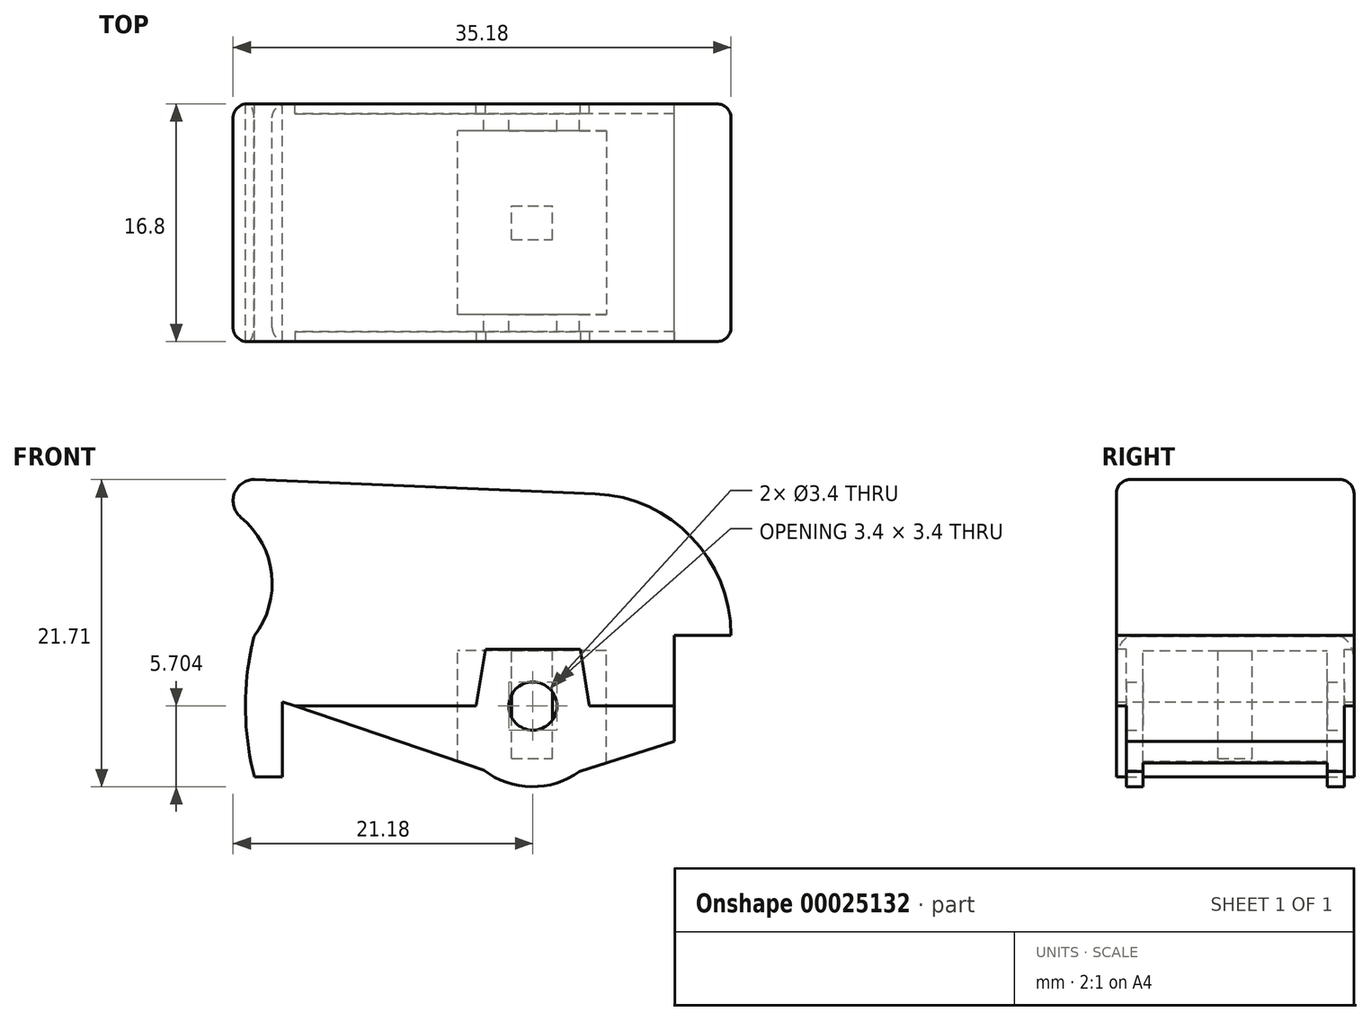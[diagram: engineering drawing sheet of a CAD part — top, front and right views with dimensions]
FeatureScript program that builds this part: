
annotation { "Feature Type Name" : "Feature", "Feature Type Description" : "" }
export const myFeature = defineFeature(function(context is Context, id is Id, definition is map)
    precondition{}
    {
        {
            var Q0;
            Q0=qCreatedBy(makeId("Front.planeOp"),FACE);
            var sketch = newSketch(context, id + "F0", { "sketchPlane" : qUnion([Q0])});
            skLineSegment(sketch, "E0", {"start": v(-33.61, 31.26) * mm, "end": v(-9.6, 30.25) * mm});
            skArc(sketch, "E1", {"start": v(0, 20.25) * mm, "mid": v(-2.78, 27.18) * mm, "end": v(-9.6, 30.25) * mm});
            skLineSegment(sketch, "E2", {"start": v(0, 20.25) * mm, "end": v(-4, 20.25) * mm});
            skLineSegment(sketch, "E3", {"start": v(-4, 20.25) * mm, "end": v(-4, 12.75) * mm});
            skLineSegment(sketch, "E4", {"start": v(-4, 15.25) * mm, "end": v(-26.9, 15.25) * mm, "construction": true});
            skCircle(sketch, "E5", {"center": v(-14, 15.25) * mm, "radius": 1.7 * mm});
            skArc(sketch, "E6", {"start": v(-33.7, 20.18) * mm, "mid": v(-34.3, 15.22) * mm, "end": v(-33.68, 10.26) * mm});
            skArc(sketch, "E7.0", {"start": v(-17.47, 10.73) * mm, "mid": v(-14.1, 9.55) * mm, "end": v(-10.7, 10.61) * mm});
            skPoint(sketch, "E8.visualSharp", {"position": v(-29.1, 31.07) * mm});
            skArc(sketch, "E8.filletArc", {"start": v(-33.61, 31.26) * mm, "mid": v(-35.08, 30.3) * mm, "end": v(-34.63, 28.6) * mm});
            skArc(sketch, "E9", {"start": v(-34.63, 28.6) * mm, "mid": v(-32.45, 24.58) * mm, "end": v(-33.7, 20.18) * mm});
            skLineSegment(sketch, "E10", {"start": v(-33.61, 31.26) * mm, "end": v(-33.68, 10.26) * mm, "construction": true});
            skLineSegment(sketch, "E11", {"start": v(-33.68, 10.26) * mm, "end": v(-31.68, 10.25) * mm});
            skLineSegment(sketch, "E12", {"start": v(-31.68, 10.25) * mm, "end": v(-31.68, 15.55) * mm});
            skLineSegment(sketch, "E13", {"start": v(-31.68, 15.55) * mm, "end": v(-17.47, 10.73) * mm});
            skLineSegment(sketch, "E14", {"start": v(-4, 12.75) * mm, "end": v(-10.7, 10.61) * mm});
            skPoint(sketch, "E15.orphan", {"position": v(-14, 9.55) * mm});
            skSolve(sketch);
        }
        {
            var Q0;
            Q0=makeQuery(id+"F0.imprint","IMPRINT",FACE,{"disambiguationData":[TD([[makeQuery(id+"F0.imprint","IMPRINT",EDGE,{"derivedFrom":sQuery(id+"F0.wireOp",EDGE,"E0")}),-1.0]])]});
            extrude(context, id + "F1", {"entities" : qUnion([Q0]), "depth" : 16.8 / 2 * mm, "hasSecondDirection" : true, "secondDirectionOppositeDirection" : true, "secondDirectionDepth" : (16.8 / 2) * mm});
        }
        {
            var Q0;
            Q0=makeQuery(id+"F1.opExtrude","CAP_FACE",FACE,{"disambiguationData":[OSD([sQuery(id+"F0.wireOp",EDGE,"E0"),sQuery(id+"F0.wireOp",EDGE,"E1"),sQuery(id+"F0.wireOp",EDGE,"E2"),sQuery(id+"F0.wireOp",EDGE,"E3"),sQuery(id+"F0.wireOp",EDGE,"E5"),sQuery(id+"F0.wireOp",EDGE,"E6"),sQuery(id+"F0.wireOp",EDGE,"E7.0"),sQuery(id+"F0.wireOp",EDGE,"E8.filletArc"),sQuery(id+"F0.wireOp",EDGE,"E9"),sQuery(id+"F0.wireOp",EDGE,"E11"),sQuery(id+"F0.wireOp",EDGE,"E12"),sQuery(id+"F0.wireOp",EDGE,"E13"),sQuery(id+"F0.wireOp",EDGE,"E14")])],"isStart":false});
            var sketch = newSketch(context, id + "F2", { "sketchPlane" : qUnion([Q0])});
            skLineSegment(sketch, "E16", {"start": v(-4, 15.25) * mm, "end": v(-10, 15.25) * mm});
            skLineSegment(sketch, "E17", {"start": v(-10, 15.25) * mm, "end": v(-10.65, 19.25) * mm});
            skLineSegment(sketch, "E18", {"start": v(-10.65, 19.25) * mm, "end": v(-17.35, 19.25) * mm});
            skLineSegment(sketch, "E19", {"start": v(-17.35, 19.25) * mm, "end": v(-18, 15.25) * mm});
            skLineSegment(sketch, "E20", {"start": v(-18, 15.25) * mm, "end": v(-30.8, 15.25) * mm});
            skLineSegment(sketch, "E21", {"start": v(-14, 15.25) * mm, "end": v(-14, 19.25) * mm, "construction": true});
            skSolve(sketch);
        }
        {
            var Q0;
            {var subQ4=sQuery(id+"F2.wireOp",EDGE,"E16");Q0=makeQuery(id+"F2.imprint","IMPRINT",FACE,{"disambiguationData":[TD([[makeQuery(id+"F2.imprint","IMPRINT",EDGE,{"derivedFrom":subQ4}),1.0]])]});}
            extrude(context, id + "F3", {"entities" : qUnion([Q0]), "oppositeDirection" : true, "depth" : 0.7 * mm});
        }
        {
            var Q0;
            Q0=makeQuery(id+"F3.opExtrude","SWEPT_BODY",BODY,{"disambiguationData":[OSD([sQuery(id+"F0.wireOp",EDGE,"E3"),sQuery(id+"F0.wireOp",EDGE,"E5"),sQuery(id+"F0.wireOp",EDGE,"E7.0"),sQuery(id+"F0.wireOp",EDGE,"E13"),sQuery(id+"F0.wireOp",EDGE,"E14"),sQuery(id+"F2.wireOp",EDGE,"E16"),sQuery(id+"F2.wireOp",EDGE,"E17"),sQuery(id+"F2.wireOp",EDGE,"E18"),sQuery(id+"F2.wireOp",EDGE,"E19"),sQuery(id+"F2.wireOp",EDGE,"E20")])]});
            var Q1;
            Q1=qCreatedBy(makeId("Front.planeOp"),FACE);
            mirror(context, id + "F4", {"entities" : qUnion([Q0]), "mirrorPlane" : qUnion([Q1])});
        }
        {
            var Q0;
            Q0=makeQuery(id+"F3.opExtrude","SWEPT_BODY",BODY,{"disambiguationData":[OSD([sQuery(id+"F0.wireOp",EDGE,"E3"),sQuery(id+"F0.wireOp",EDGE,"E5"),sQuery(id+"F0.wireOp",EDGE,"E7.0"),sQuery(id+"F0.wireOp",EDGE,"E13"),sQuery(id+"F0.wireOp",EDGE,"E14"),sQuery(id+"F2.wireOp",EDGE,"E16"),sQuery(id+"F2.wireOp",EDGE,"E17"),sQuery(id+"F2.wireOp",EDGE,"E18"),sQuery(id+"F2.wireOp",EDGE,"E19"),sQuery(id+"F2.wireOp",EDGE,"E20")])]});
            var Q1;
            Q1=makeQuery(id+"F4.opPattern","COPY",BODY,{"derivedFrom":makeQuery(id+"F3.opExtrude","SWEPT_BODY",BODY,{"disambiguationData":[OSD([sQuery(id+"F0.wireOp",EDGE,"E3"),sQuery(id+"F0.wireOp",EDGE,"E5"),sQuery(id+"F0.wireOp",EDGE,"E7.0"),sQuery(id+"F0.wireOp",EDGE,"E13"),sQuery(id+"F0.wireOp",EDGE,"E14"),sQuery(id+"F2.wireOp",EDGE,"E16"),sQuery(id+"F2.wireOp",EDGE,"E17"),sQuery(id+"F2.wireOp",EDGE,"E18"),sQuery(id+"F2.wireOp",EDGE,"E19"),sQuery(id+"F2.wireOp",EDGE,"E20")])]}),"instanceName":"1"});
            var Q2;
            Q2=makeQuery(id+"F1.opExtrude","SWEPT_BODY",BODY,{"disambiguationData":[OSD([sQuery(id+"F0.wireOp",EDGE,"E0"),sQuery(id+"F0.wireOp",EDGE,"E1"),sQuery(id+"F0.wireOp",EDGE,"E2"),sQuery(id+"F0.wireOp",EDGE,"E3"),sQuery(id+"F0.wireOp",EDGE,"E5"),sQuery(id+"F0.wireOp",EDGE,"E6"),sQuery(id+"F0.wireOp",EDGE,"E7.0"),sQuery(id+"F0.wireOp",EDGE,"E8.filletArc"),sQuery(id+"F0.wireOp",EDGE,"E9"),sQuery(id+"F0.wireOp",EDGE,"E11"),sQuery(id+"F0.wireOp",EDGE,"E12"),sQuery(id+"F0.wireOp",EDGE,"E13"),sQuery(id+"F0.wireOp",EDGE,"E14")])]});
            booleanBodies(context, id + "F5", {"operationType" : BooleanOperationType.SUBTRACTION, "tools" : qUnion([Q0, Q1]), "targets" : qUnion([Q2])});
        }
        {
            var Q0;
            Q0=makeQuery(id+"F5.opBoolean","COPY",FACE,{"derivedFrom":makeQuery(id+"F3.opExtrude","SWEPT_FACE",FACE,{"disambiguationData":[OSD([sQuery(id+"F2.wireOp",EDGE,"E16")])]})});
            var sketch = newSketch(context, id + "F6", { "sketchPlane" : qUnion([Q0])});
            skLineSegment(sketch, "E22.bottom", {"start": v(-8.8, 6.5) * mm, "end": v(-19.3, 6.5) * mm});
            skLineSegment(sketch, "E22.top", {"start": v(-8.8, -6.5) * mm, "end": v(-19.3, -6.5) * mm});
            skLineSegment(sketch, "E22.left", {"start": v(-8.8, 6.5) * mm, "end": v(-8.8, -6.5) * mm});
            skLineSegment(sketch, "E22.right", {"start": v(-19.3, 6.5) * mm, "end": v(-19.3, -6.5) * mm});
            skSolve(sketch);
        }
        {
            var Q0;
            Q0 = qSketchRegion(id + "F6", true);
            extrude(context, id + "F7", {"entities" : qUnion([Q0]), "operationType" : NewBodyOperationType.REMOVE, "endBound" : BoundingType.THROUGH_ALL, "depth" : 25 * mm, "hasSecondDirection" : true, "secondDirectionOppositeDirection" : true, "secondDirectionDepth" : (6.4 - 2.5) * mm});
        }
        {
            var Q0;
            Q0=makeQuery(id+"F7.boolean.opBoolean","COPY",FACE,{"derivedFrom":makeQuery(id+"F7.opExtrude","CAP_FACE",FACE,{"disambiguationData":[OSD([sQuery(id+"F6.wireOp",EDGE,"E22.bottom"),sQuery(id+"F6.wireOp",EDGE,"E22.top"),sQuery(id+"F6.wireOp",EDGE,"E22.left"),sQuery(id+"F6.wireOp",EDGE,"E22.right")])],"isStart":true})});
            var sketch = newSketch(context, id + "F8", { "sketchPlane" : qUnion([Q0])});
            skLineSegment(sketch, "E23.bottom", {"start": v(-15.5, 1.2) * mm, "end": v(-12.6, 1.2) * mm});
            skLineSegment(sketch, "E23.top", {"start": v(-15.5, -1.2) * mm, "end": v(-12.6, -1.2) * mm});
            skLineSegment(sketch, "E23.left", {"start": v(-15.5, 1.2) * mm, "end": v(-15.5, -1.2) * mm});
            skLineSegment(sketch, "E23.right", {"start": v(-12.6, 1.2) * mm, "end": v(-12.6, -1.2) * mm});
            skLineSegment(sketch, "E24", {"start": v(-14.05, 1.2) * mm, "end": v(-14.05, -1.2) * mm, "construction": true});
            skLineSegment(sketch, "E25", {"start": v(-14.05, 0) * mm, "end": v(-19.3, 0) * mm, "construction": true});
            skLineSegment(sketch, "E26", {"start": v(-14.05, 0) * mm, "end": v(-14.05, -6.5) * mm, "construction": true});
            skPoint(sketch, "E27.orphan", {"position": v(-14.05, 6.5) * mm});
            skPoint(sketch, "E28.orphan", {"position": v(-8.8, 0) * mm});
            skSolve(sketch);
        }
        {
            var Q0;
            Q0=makeQuery(id+"F8.imprint","IMPRINT",FACE,{"disambiguationData":[TD([[makeQuery(id+"F8.imprint","IMPRINT",EDGE,{"derivedFrom":sQuery(id+"F8.wireOp",EDGE,"E23.bottom")}),-1.0]])]});
            extrude(context, id + "F9", {"entities" : qUnion([Q0]), "operationType" : NewBodyOperationType.ADD, "depth" : 7.6 * mm});
        }
        {
            var Q0;
            Q0=makeQuery(id+"F1.opExtrude","CAP_EDGE",EDGE,{"disambiguationData":[OSD([sQuery(id+"F0.wireOp",EDGE,"E1")])],"isStart":false});
            fillet(context, id + "F10", {"entities" : qUnion([Q0]), "radius" : 1 * mm, "tangentPropagation" : true, "allowEdgeOverflow" : false});
        }
        {
            var Q0;
            Q0=makeQuery(id+"F1.opExtrude","CAP_EDGE",EDGE,{"disambiguationData":[OSD([sQuery(id+"F0.wireOp",EDGE,"E1")])],"isStart":true});
            fillet(context, id + "F11", {"entities" : qUnion([Q0]), "radius" : 1 * mm, "tangentPropagation" : true, "allowEdgeOverflow" : false});
        }
    });
